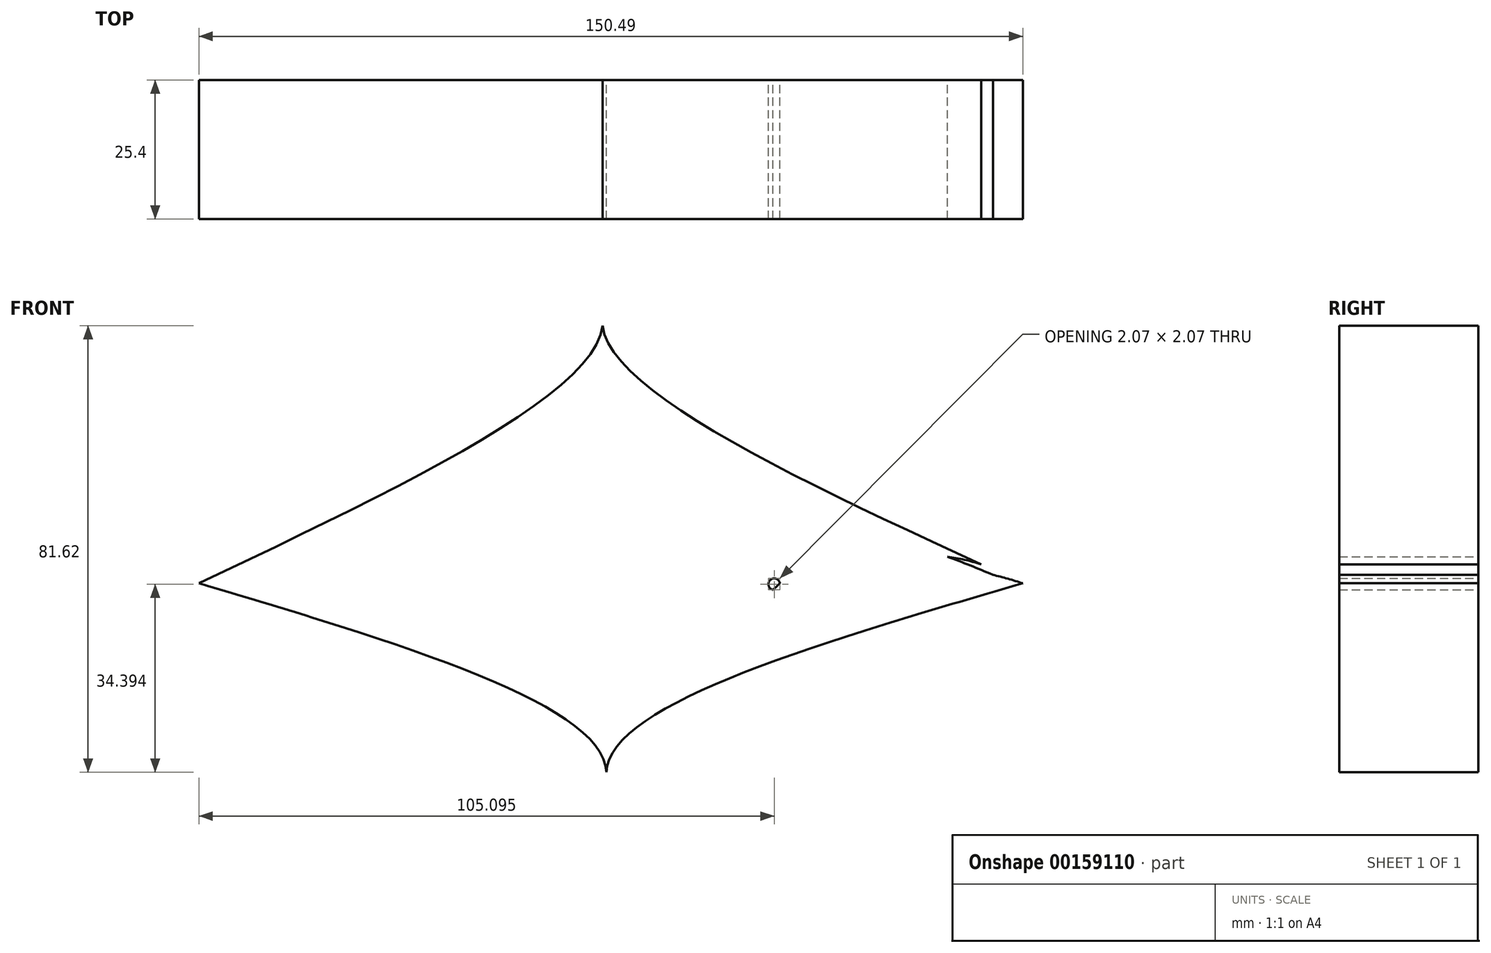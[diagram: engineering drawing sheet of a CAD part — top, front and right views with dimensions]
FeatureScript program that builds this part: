
annotation { "Feature Type Name" : "Feature", "Feature Type Description" : "" }
export const myFeature = defineFeature(function(context is Context, id is Id, definition is map)
    precondition{}
    {
        {
            var Q0;
            Q0=qCreatedBy(makeId("Front.planeOp"),FACE);
            var sketch = newSketch(context, id + "F0", { "sketchPlane" : qUnion([Q0])});
            skFitSpline(sketch, "E0", {"points": [v(-75.52, -75.8) * mm, v(0, -34.55) * mm, v(-74.42, 0) * mm], "startDerivative": vector(225.13, 84.44) * mm, "endDerivative": vector(-224.71, 67.07) * mm});
            skFitSpline(sketch, "E1", {"points": [v(76.07, -75.61) * mm, v(0, -34.55) * mm, v(76.07, 0) * mm], "startDerivative": vector(-227.58, 84.38) * mm, "endDerivative": vector(228.87, 66.8) * mm});
            skLineSegment(sketch, "E2", {"start": v(-11.83, 35.53) * mm, "end": v(-11.83, 35.53) * mm});
            skLineSegment(sketch, "E3.trimOffspring", {"start": v(-0.7, 48.52) * mm, "end": v(-0.7, 48.52) * mm});
            skLineSegment(sketch, "E4.trimOffspring", {"start": v(0, 51.42) * mm, "end": v(0, 51.42) * mm});
            skPoint(sketch, "E5.2.internal.orphan", {"position": v(30.24, 76.71) * mm});
            skPoint(sketch, "E5.3.internal.orphan", {"position": v(29.88, 76.71) * mm});
            skFitSpline(sketch, "E6", {"points": [v(-74.42, 0) * mm, v(-0.7, 48.52) * mm, v(-76.25, 75.98) * mm], "startDerivative": vector(220.5, 104.7) * mm, "endDerivative": vector(-227.66, 46.8) * mm});
            skFitSpline(sketch, "E7", {"points": [v(76.07, 0) * mm, v(-0.7, 48.52) * mm, v(76.07, 75.98) * mm], "startDerivative": vector(-228.42, 104.26) * mm, "endDerivative": vector(232.56, 47.19) * mm});
            skArc(sketch, "E8", {"start": v(-28.04, 0) * mm, "mid": v(1.83, -12.09) * mm, "end": v(31.71, 0) * mm});
            skArc(sketch, "E9", {"start": v(31.71, 0) * mm, "mid": v(29.94, 0.62) * mm, "end": v(30.43, -1.2) * mm});
            skArc(sketch, "E10", {"start": v(76.07, 0) * mm, "mid": v(52.9, 3.72) * mm, "end": v(29.7, 0.27) * mm});
            skArc(sketch, "E11", {"start": v(-28.04, 0) * mm, "mid": v(-50.45, 2.77) * mm, "end": v(-72.8, -0.49) * mm});
            skArc(sketch, "E12", {"start": v(70.6, 1.55) * mm, "mid": v(1.02, 15.64) * mm, "end": v(-68.37, 0.64) * mm});
            skArc(sketch, "E13", {"start": v(76.07, 0) * mm, "mid": v(69.45, 3.14) * mm, "end": v(62.32, 4.86) * mm});
            skArc(sketch, "E14", {"start": v(-72.8, -0.49) * mm, "mid": v(1.68, -13.75) * mm, "end": v(76.07, 0) * mm});
            skSolve(sketch);
        }
        {
            var Q0;
            {var subQ0=sQuery(id+"F0.wireOp",EDGE,"E1");var subQ1=sQuery(id+"F0.wireOp",EDGE,"E0");var subQ2=makeQuery(id+"F0.imprint","INTERSECT",VERTEX,{"disambiguationData":[OD(1.0)],"derivedFrom":[subQ1,subQ0]});Q0=makeQuery(id+"F0.imprint","IMPRINT",FACE,{"disambiguationData":[TD([[makeQuery(id+"F0.imprint","IMPRINT",EDGE,{"disambiguationData":[TD([[subQ2,-1.0]])],"derivedFrom":subQ1}),-1.0]])]});}
            var Q1;
            {var subQ1=sQuery(id+"F0.wireOp",EDGE,"E6");var subQ5=sQuery(id+"F0.wireOp",EDGE,"E0");var subQ6=makeQuery(id+"F0.imprint","INTERSECT",VERTEX,{"derivedFrom":[subQ5,subQ1]});Q1=makeQuery(id+"F0.imprint","IMPRINT",FACE,{"disambiguationData":[TD([[makeQuery(id+"F0.imprint","IMPRINT",EDGE,{"disambiguationData":[TD([[subQ6,-1.0]])],"derivedFrom":subQ1}),-1.0]])]});}
            var Q2;
            {var subQ1=sQuery(id+"F0.wireOp",EDGE,"E8");var subQ11=sQuery(id+"F0.wireOp",EDGE,"E11");var subQ12=makeQuery(id+"F0.imprint","INTERSECT",VERTEX,{"derivedFrom":[subQ1,subQ11]});Q2=makeQuery(id+"F0.imprint","IMPRINT",FACE,{"disambiguationData":[TD([[makeQuery(id+"F0.imprint","IMPRINT",EDGE,{"disambiguationData":[TD([[subQ12,-1.0]])],"derivedFrom":subQ1}),-1.0]])]});}
            var Q3;
            {var subQ5=sQuery(id+"F0.wireOp",EDGE,"E8");var subQ8=sQuery(id+"F0.wireOp",EDGE,"E11");var subQ9=makeQuery(id+"F0.imprint","INTERSECT",VERTEX,{"derivedFrom":[subQ5,subQ8]});Q3=makeQuery(id+"F0.imprint","IMPRINT",FACE,{"disambiguationData":[TD([[makeQuery(id+"F0.imprint","IMPRINT",EDGE,{"disambiguationData":[TD([[subQ9,-1.0]])],"derivedFrom":subQ5}),1.0]])]});}
            extrude(context, id + "F1", {"entities" : qUnion([Q0, Q1, Q2, Q3]), "depth" : 25.4 * mm});
        }
    });
